# Revit family: 402_VCE-B-150-V-ZP-0-0
name_source: partatom
category: Mechanical Equipment
revit_build: Autodesk Revit 2018 (Build: 20170223_1515(x64)
units: mm (PartAtom-declared; Revit-internal decimal feet)

## family parameters
Always vertical = Yes
Cut with Voids When Loaded = No
Part Type = Normal
Room Calculation Point = No
Round Connector Dimension = Use Diameter
Shared = No
Work Plane-Based = No

## types (1)
- VCE-B-150-V-ZP-0-0
    Description = Air curtain ESSENSSE B, length 1,5m, water heater
    H = 179 mm  [stored 0.58727 ft]
    L = 1530 mm  [stored 5.01969 ft]
    L2 = 765 mm  [stored 2.50984 ft]
    L3 = 715 mm  [stored 2.3458 ft]
    L__ve = -1530 mm  [stored -5.01969 ft]
    MC Product Code = VCE-B-150-V-ZP-0-0
    MT1 = Yes
    MT2 = No
    Manufacturer = 2VV
    QmdConnectorList = 331;PHS;361;PHR
    R1 = 90 mm
    URL = www.2vv.cz
    W2 = 186 mm
    W3 = 96 mm  [stored 0.314961 ft]
    Y1 = 20 mm  [stored 0.0656168 ft]
    magiPartTypeId = 402
    magiProductFamilyId = VCE-B-150-V-ZP-0-0
    magiProductId = VCE-B-150-V-ZP-0-0

note: [stored X ft] marks values corroborated as IEEE doubles in the binary element streams (Revit-internal decimal feet)

## geometry (parser evidence)
native form markers: Blend x2, Sweep x3
no freeform markers — native parametric forms only
